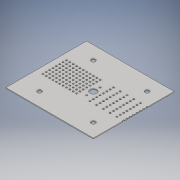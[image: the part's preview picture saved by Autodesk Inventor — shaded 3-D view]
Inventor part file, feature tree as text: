
AUTODESK INVENTOR PART (.ipt)
format: ipt  version: 2018 (Build 220112000, 112)  size: 377,856 bytes
history: native  units: in
note: dims shown in document units (in); Inventor stores cm internally (conversion verified against a paired STEP export)
features: extrude x5, sketch x5
ambient origin geometry x8: Origin, YZ Plane, XZ Plane, XY Plane, X Axis, Y Axis, Z Axis, Center Point
bodies: Solid1 (feature_tree)
feature tree (10):
  extrude  "Extrusion1"  Depth=0.125in
  extrude  "Extrusion2"  Depth=2.0in TaperAngle=0.0deg
  sketch  "Sketch3"  dims[d9=0.25in d11=0.25in]
  sketch  "Sketch4"  dims[d12=0.25in d13=0.25in d14=0.25in d15=0.25in]
  extrude  "Extrusion5"  Depth=0.25in
  extrude  "Extrusion8"  Depth=0.25in
  extrude  "Extrusion9"  Depth=0.5in
  sketch  "Sketch1"  dims[d2=0.125in d3=0.0in d4=6.0in]
  sketch  "Sketch2"  dims[d5=1.0in d6=2.0in d7=0.0in]
  sketch  "Sketch5"  dims[d56=0.25in d63=0.625in d67=8.0in d69=0.625in d70=0.625in d71=36.0in d72=0.0in d73=13.0in d74=13.0in d75=12.0in d77=0.25in d78=0.25in d79=0.25in d80=0.25in d81=0.25in d82=0.25in d83=0.5in d84=0.5in d85=0.5in d86=0.5in d87=0.5in d88=0.5in d89=0.25in d90=0.25in d91=0.25in d92=0.25in d93=0.25in d94=0.25in d95=0.25in d96=0.25in d97=0.25in d98=0.25in d99=0.25in d100=0.25in d101=0.25in d102=0.25in d103=0.25in d104=0.25in d105=0.25in d106=0.25in d107=0.25in d108=0.25in d109=0.25in d110=0.25in d111=0.25in d112=0.25in d113=0.5in d114=0.25in d115=0.25in d116=0.25in d117=0.25in d118=0.25in d119=0.25in d120=0.5in d121=0.25in d122=0.25in d123=0.25in d124=0.25in d125=0.25in d126=0.25in d127=0.5in d128=0.5in d130=0.25in d135=3.0in d136=0.0in d137=0.5in d138=0.5in d139=0.5in d140=0.5in d141=0.5in d142=0.5in d143=0.5in d144=0.5in d145=0.5in d146=0.5in d147=0.5in d148=0.5in d149=0.5in d150=0.5in d151=0.5in d152=0.5in d153=0.5in d154=0.5in d155=0.5in d156=0.5in d157=0.5in d158=0.5in d159=0.5in d160=0.5in d161=0.5in d162=0.5in d163=0.5in d164=0.5in d165=0.5in d166=0.5in d167=0.5in d168=0.5in d169=0.5in d170=0.5in d171=0.5in d172=0.5in d173=0.5in d174=0.5in d175=0.5in d176=0.5in d177=0.5in d178=0.5in d179=0.5in d180=0.5in d181=0.5in d182=3.0in d183=0.0in]
